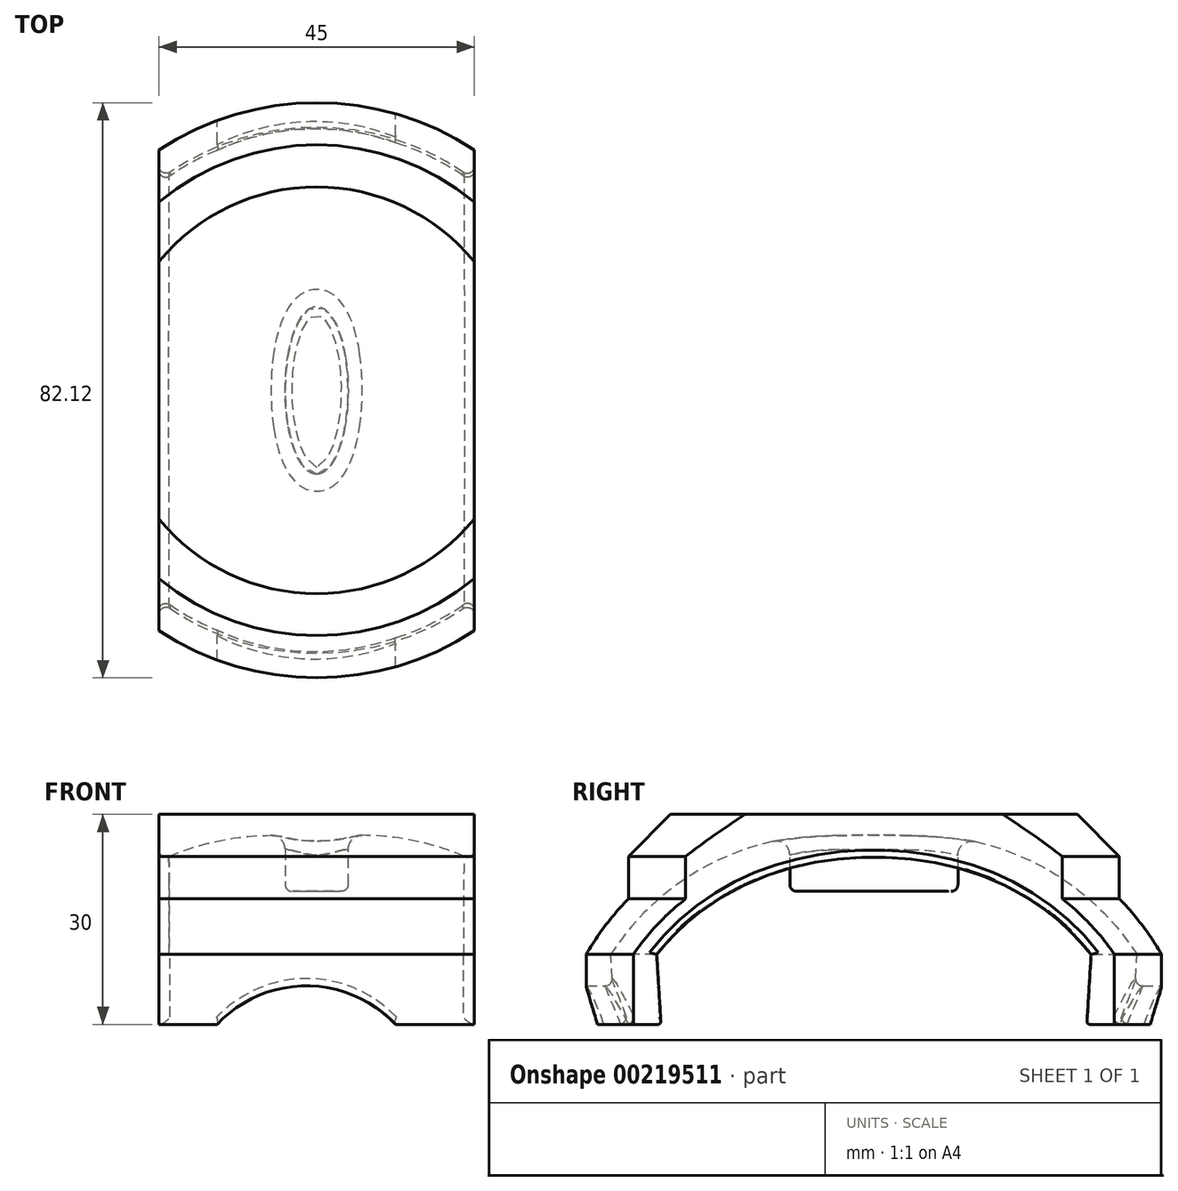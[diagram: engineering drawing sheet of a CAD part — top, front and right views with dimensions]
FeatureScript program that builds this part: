
annotation { "Feature Type Name" : "Feature", "Feature Type Description" : "" }
export const myFeature = defineFeature(function(context is Context, id is Id, definition is map)
    precondition{}
    {
        {
            var Q0;
            Q0=qCreatedBy(makeId("Top.planeOp"),FACE);
            var sketch = newSketch(context, id + "F0", { "sketchPlane" : qUnion([Q0])});
            skCircle(sketch, "E0", {"center": v(0, 0) * mm, "radius": 37.55 * mm});
            skSolve(sketch);
        }
        {
            var Q0;
            Q0=makeQuery(id+"F0.imprint","IMPRINT",FACE,{"disambiguationData":[TD([[makeQuery(id+"F0.imprint","IMPRINT",EDGE,{"derivedFrom":sQuery(id+"F0.wireOp",EDGE,"E0")}),1.0]])]});
            extrude(context, id + "F1", {"entities" : qUnion([Q0]), "depth" : 17 * mm});
        }
        {
            var Q0;
            Q0=makeQuery(id+"F1.opExtrude","CAP_EDGE",EDGE,{"disambiguationData":[OSD([sQuery(id+"F0.wireOp",EDGE,"E0")])],"isStart":false});
            fillet(context, id + "F2", {"entities" : qUnion([Q0]), "radius" : 37 * mm, "tangentPropagation" : true, "allowEdgeOverflow" : false});
        }
        {
            var Q0;
            Q0=makeQuery(id+"F1.opExtrude","CAP_FACE",FACE,{"disambiguationData":[OSD([sQuery(id+"F0.wireOp",EDGE,"E0")])],"isStart":true});
            shell(context, id + "F3", {"entities" : qUnion([Q0]), "thickness" : 3 * mm, "oppositeDirection" : true});
        }
        {
            var Q0;
            {var subQ0=sQuery(id+"F0.wireOp",EDGE,"E0");Q0=makeQuery(id+"F3.opShell","OFFSET_FACE",FACE,{"disambiguationData":[OSD([subQ0]),TDD([makeQuery(id+"F1.opExtrude","CAP_FACE",FACE,{"disambiguationData":[OSD([subQ0])],"isStart":false})])]});}
            var sketch = newSketch(context, id + "F4", { "sketchPlane" : qUnion([Q0])});
            skEllipse(sketch, "E1", {"center": v(0, 0) * mm, "majorRadius": 12 * mm, "minorRadius": 4.5 * mm, "majorAxis": v(0, 1)});
            skSolve(sketch);
        }
        {
            var Q0;
            {var subQ0=sQuery(id+"F4.wireOp",EDGE,"E1");var subQ1=sQuery(id+"F0.wireOp",EDGE,"E0");var subQ2=makeQuery(id+"F3.opShell","OFFSET_EDGE",EDGE,{"disambiguationData":[OSD([subQ1]),TDD([makeQuery(id+"F2.opFillet","BLEND_EDGE",EDGE,{"blendedFrom":[makeQuery(id+"F1.opExtrude","CAP_EDGE",EDGE,{"disambiguationData":[OSD([subQ1])],"isStart":false}),makeQuery(id+"F1.opExtrude","CAP_FACE",FACE,{"disambiguationData":[OSD([subQ1])],"isStart":false})],"blendedInto":[makeQuery(id+"F1.opExtrude","CAP_FACE",FACE,{"disambiguationData":[OSD([subQ1])],"isStart":false})]})])]});var subQ3=makeQuery(id+"F4.imprint","INTERSECT",VERTEX,{"disambiguationData":[OD(0.0)],"derivedFrom":[subQ2,subQ0]});Q0=makeQuery(id+"F4.imprint","IMPRINT",FACE,{"disambiguationData":[TD([[makeQuery(id+"F4.imprint","IMPRINT",EDGE,{"disambiguationData":[TD([[subQ3,-1.0]])],"derivedFrom":subQ0}),1.0]])]});}
            var Q1;
            {var subQ0=sQuery(id+"F4.wireOp",EDGE,"E1");var subQ1=sQuery(id+"F0.wireOp",EDGE,"E0");var subQ2=makeQuery(id+"F3.opShell","OFFSET_EDGE",EDGE,{"disambiguationData":[OSD([subQ1]),TDD([makeQuery(id+"F2.opFillet","BLEND_EDGE",EDGE,{"blendedFrom":[makeQuery(id+"F1.opExtrude","CAP_EDGE",EDGE,{"disambiguationData":[OSD([subQ1])],"isStart":false}),makeQuery(id+"F1.opExtrude","CAP_FACE",FACE,{"disambiguationData":[OSD([subQ1])],"isStart":false})],"blendedInto":[makeQuery(id+"F1.opExtrude","CAP_FACE",FACE,{"disambiguationData":[OSD([subQ1])],"isStart":false})]})])]});var subQ3=makeQuery(id+"F4.imprint","INTERSECT",VERTEX,{"disambiguationData":[OD(0.0)],"derivedFrom":[subQ2,subQ0]});Q1=makeQuery(id+"F4.imprint","IMPRINT",FACE,{"disambiguationData":[TD([[makeQuery(id+"F4.imprint","IMPRINT",EDGE,{"disambiguationData":[TD([[subQ3,1.0]])],"derivedFrom":subQ0}),1.0]])]});}
            var Q2;
            {var subQ0=sQuery(id+"F4.wireOp",EDGE,"E1");var subQ1=sQuery(id+"F0.wireOp",EDGE,"E0");var subQ2=makeQuery(id+"F3.opShell","OFFSET_EDGE",EDGE,{"disambiguationData":[OSD([subQ1]),TDD([makeQuery(id+"F2.opFillet","BLEND_EDGE",EDGE,{"blendedFrom":[makeQuery(id+"F1.opExtrude","CAP_EDGE",EDGE,{"disambiguationData":[OSD([subQ1])],"isStart":false}),makeQuery(id+"F1.opExtrude","CAP_FACE",FACE,{"disambiguationData":[OSD([subQ1])],"isStart":false})],"blendedInto":[makeQuery(id+"F1.opExtrude","CAP_FACE",FACE,{"disambiguationData":[OSD([subQ1])],"isStart":false})]})])]});var subQ3=makeQuery(id+"F4.imprint","INTERSECT",VERTEX,{"disambiguationData":[OD(1.0)],"derivedFrom":[subQ2,subQ0]});Q2=makeQuery(id+"F4.imprint","IMPRINT",FACE,{"disambiguationData":[TD([[makeQuery(id+"F4.imprint","IMPRINT",EDGE,{"disambiguationData":[TD([[subQ3,1.0]])],"derivedFrom":subQ0}),1.0]])]});}
            extrude(context, id + "F5", {"entities" : qUnion([Q0, Q1, Q2]), "operationType" : NewBodyOperationType.ADD, "depth" : 8 * mm});
        }
        {
            var Q0;
            Q0=makeQuery(id+"F1.opExtrude","CAP_FACE",FACE,{"disambiguationData":[OSD([sQuery(id+"F0.wireOp",EDGE,"E0")])],"isStart":true});
            var sketch = newSketch(context, id + "F6", { "sketchPlane" : qUnion([Q0])});
            skLineSegment(sketch, "E2", {"start": v(0, -41.06) * mm, "end": v(0, -41.06) * mm});
            skLineSegment(sketch, "E3", {"start": v(0, -41.06) * mm, "end": v(0, 41.06) * mm, "construction": true});
            skLineSegment(sketch, "E4", {"start": v(0, 0) * mm, "end": v(37.55, 0) * mm, "construction": true});
            skLineSegment(sketch, "E5", {"start": v(0, 0) * mm, "end": v(-37.55, 0) * mm, "construction": true});
            skLineSegment(sketch, "E6", {"start": v(0, 0) * mm, "end": v(12.69, 39.05) * mm, "construction": true});
            skLineSegment(sketch, "E7", {"start": v(0, 0) * mm, "end": v(-12.69, -39.05) * mm, "construction": true});
            skLineSegment(sketch, "E8", {"start": v(0, 0) * mm, "end": v(-12.69, 39.05) * mm, "construction": true});
            skLineSegment(sketch, "E9", {"start": v(0, 0) * mm, "end": v(12.69, -39.05) * mm, "construction": true});
            skLineSegment(sketch, "E10", {"start": v(37.55, 0) * mm, "end": v(41.06, 0) * mm, "construction": true});
            skLineSegment(sketch, "E11", {"start": v(-37.55, 0) * mm, "end": v(-41.06, 0) * mm, "construction": true});
            skSolve(sketch);
        }
        {
            var Q0;
            Q0=qCreatedBy(makeId("Front.planeOp"),FACE);
            var sketch = newSketch(context, id + "F7", { "sketchPlane" : qUnion([Q0])});
            skLineSegment(sketch, "E12", {"start": v(41.06, 0) * mm, "end": v(41.06, -10) * mm});
            skLineSegment(sketch, "E13", {"start": v(41.06, -10) * mm, "end": v(37.55, -10) * mm});
            skLineSegment(sketch, "E14", {"start": v(37.05, -10) * mm, "end": v(37.55, 0) * mm});
            skLineSegment(sketch, "E15", {"start": v(37.55, 0) * mm, "end": v(41.06, 0) * mm});
            skLineSegment(sketch, "E16", {"start": v(37.55, 0) * mm, "end": v(37.55, -10) * mm});
            skLineSegment(sketch, "E17", {"start": v(37.55, -10) * mm, "end": v(37.05, -10) * mm});
            skLineSegment(sketch, "E18", {"start": v(0, 0) * mm, "end": v(0, -14.5) * mm, "construction": true});
            skSolve(sketch);
        }
        {
            var Q0;
            {var subQ0=makeQuery(id+"FDc1g6xEYOhVyaV_1.opRevolve","SWEPT_EDGE",EDGE,{"disambiguationData":[OSD([sQuery(id+"F7.wireOp",EDGE,"E12"),sQuery(id+"F7.wireOp",EDGE,"E13")])]});Q0=makeQuery(id+"FIxkV1x1mZ7Anp5_2.boolean.opBoolean","MERGE",EDGE,{"derivedFrom":[subQ0,makeQuery(id+"FIxkV1x1mZ7Anp5_2.opPattern","COPY",EDGE,{"derivedFrom":subQ0,"instanceName":"1"})]});}
            var Q1;
            Q1=makeQuery(id+"F5.opExtrude","CAP_EDGE",EDGE,{"disambiguationData":[OSD([sQuery(id+"F4.wireOp",EDGE,"E1")])],"isStart":false});
            fillet(context, id + "F8", {"entities" : qUnion([Q0, Q1]), "radius" : 1 * mm, "tangentPropagation" : true, "allowEdgeOverflow" : false});
        }
        {
            var Q0;
            Q0=makeQuery(id+"F1.opExtrude","CAP_FACE",FACE,{"disambiguationData":[OSD([sQuery(id+"F0.wireOp",EDGE,"E0")])],"isStart":false});
            var sketch = newSketch(context, id + "F9", { "sketchPlane" : qUnion([Q0])});
            skCircle(sketch, "E19", {"center": v(0, 0) * mm, "radius": 35.05 * mm});
            skSolve(sketch);
        }
        {
            var Q0;
            Q0=makeQuery(id+"F9.imprint","IMPRINT",FACE,{"disambiguationData":[TD([[makeQuery(id+"F9.imprint","IMPRINT",EDGE,{"derivedFrom":sQuery(id+"F9.wireOp",EDGE,"E19")}),1.0]])]});
            extrude(context, id + "F10", {"entities" : qUnion([Q0]), "operationType" : NewBodyOperationType.ADD, "endBound" : BoundingType.UP_TO_NEXT, "oppositeDirection" : true, "depth" : 25 * mm});
        }
        {
            var Q0;
            Q0=makeQuery(id+"F10.opExtrude","CAP_EDGE",EDGE,{"disambiguationData":[OSD([sQuery(id+"F9.wireOp",EDGE,"E19")])],"isStart":true});
            chamfer(context, id + "F11", {"entities" : qUnion([Q0]), "width" : 6 * mm, "tangentPropagation" : true});
        }
        {
            var Q0;
            Q0=makeQuery(id+"F7.imprint","IMPRINT",FACE,{"disambiguationData":[TD([[makeQuery(id+"F7.imprint","IMPRINT",EDGE,{"derivedFrom":sQuery(id+"F7.wireOp",EDGE,"E12")}),-1.0]])]});
            var Q1;
            Q1=makeQuery(id+"F7.imprint","IMPRINT",FACE,{"disambiguationData":[TD([[makeQuery(id+"F7.imprint","IMPRINT",EDGE,{"derivedFrom":sQuery(id+"F7.wireOp",EDGE,"E14")}),-1.0]])]});
            var Q2;
            Q2=sQuery(id+"F7.wireOp",EDGE,"E18");
            revolve(context, id + "F12", {"operationType" : NewBodyOperationType.ADD, "entities" : qUnion([Q0, Q1]), "axis" : qUnion([Q2]), "revolveType" : RevolveType.FULL});
        }
        {
            var Q0;
            Q0=qCreatedBy(makeId("Right.planeOp"),FACE);
            cPlane(context, id + "F13", {"entities" : qUnion([Q0]), "cplaneType" : CPlaneType.OFFSET, "offset" : 22.5 * mm, "width" : 150 * mm, "height" : 150 * mm});
        }
        {
            var Q0;
            Q0=qCreatedBy(id+"F13.planeOp",FACE);
            var sketch = newSketch(context, id + "F14", { "sketchPlane" : qUnion([Q0])});
            skLineSegment(sketch, "E20.bottom", {"start": v(-41.47, -13.51) * mm, "end": v(42.62, -13.51) * mm});
            skLineSegment(sketch, "E20.top", {"start": v(-41.47, 26.02) * mm, "end": v(42.62, 26.02) * mm});
            skLineSegment(sketch, "E20.left", {"start": v(-41.47, -13.51) * mm, "end": v(-41.47, 26.02) * mm});
            skLineSegment(sketch, "E20.right", {"start": v(42.62, -13.51) * mm, "end": v(42.62, 26.02) * mm});
            skSolve(sketch);
        }
        {
            var Q0;
            Q0=makeQuery(id+"F14.imprint","IMPRINT",FACE,{"disambiguationData":[TD([[makeQuery(id+"F14.imprint","IMPRINT",EDGE,{"derivedFrom":sQuery(id+"F14.wireOp",EDGE,"E20.bottom")}),1.0]])]});
            extrude(context, id + "F15", {"entities" : qUnion([Q0]), "operationType" : NewBodyOperationType.REMOVE, "depth" : 25 * mm});
        }
        {
            var Q0;
            Q0=qCreatedBy(id+"F13.planeOp",FACE);
            cPlane(context, id + "F16", {"entities" : qUnion([Q0]), "cplaneType" : CPlaneType.OFFSET, "offset" : 45 * mm, "oppositeDirection" : true, "width" : 150 * mm, "height" : 150 * mm});
        }
        {
            var Q0;
            Q0=qCreatedBy(id+"F16.planeOp",FACE);
            var sketch = newSketch(context, id + "F17", { "sketchPlane" : qUnion([Q0])});
            skLineSegment(sketch, "E21.bottom", {"start": v(-41.2, -27.17) * mm, "end": v(38.42, -27.17) * mm});
            skLineSegment(sketch, "E21.top", {"start": v(-41.2, 30) * mm, "end": v(38.42, 30) * mm});
            skLineSegment(sketch, "E21.left", {"start": v(-41.2, -27.17) * mm, "end": v(-41.2, 30) * mm});
            skLineSegment(sketch, "E21.right", {"start": v(38.42, -27.17) * mm, "end": v(38.42, 30) * mm});
            skSolve(sketch);
        }
        {
            var Q0;
            Q0=makeQuery(id+"F17.imprint","IMPRINT",FACE,{"disambiguationData":[TD([[makeQuery(id+"F17.imprint","IMPRINT",EDGE,{"derivedFrom":sQuery(id+"F17.wireOp",EDGE,"E21.bottom")}),1.0]])]});
            extrude(context, id + "F18", {"entities" : qUnion([Q0]), "operationType" : NewBodyOperationType.REMOVE, "oppositeDirection" : true, "depth" : 25 * mm});
        }
        {
            var Q0;
            Q0=qCreatedBy(makeId("Front.planeOp"),FACE);
            var sketch = newSketch(context, id + "F19", { "sketchPlane" : qUnion([Q0])});
            skCircle(sketch, "E22", {"center": v(-1.48, -22) * mm, "radius": 17.5 * mm});
            skSolve(sketch);
        }
        {
            var Q0;
            Q0=makeQuery(id+"F19.imprint","IMPRINT",FACE,{"disambiguationData":[TD([[makeQuery(id+"F19.imprint","IMPRINT",EDGE,{"derivedFrom":sQuery(id+"F19.wireOp",EDGE,"E22")}),1.0]])]});
            extrude(context, id + "F20", {"entities" : qUnion([Q0]), "operationType" : NewBodyOperationType.REMOVE, "endBound" : BoundingType.SYMMETRIC, "depth" : 117.8 * mm});
        }
        {
            var Q0;
            {var subQ0=sQuery(id+"F7.wireOp",EDGE,"E17");var subQ1=sQuery(id+"F7.wireOp",EDGE,"E14");Q0=makeQuery(id+"F20.boolean.opBoolean","SPLIT",EDGE,{"disambiguationData":[TD([makeQuery(id+"F18.boolean.opBoolean","COPY",FACE,{"derivedFrom":makeQuery(id+"F18.opExtrude","CAP_FACE",FACE,{"disambiguationData":[OSD([sQuery(id+"F17.wireOp",EDGE,"E21.bottom"),sQuery(id+"F17.wireOp",EDGE,"E21.top"),sQuery(id+"F17.wireOp",EDGE,"E21.left"),sQuery(id+"F17.wireOp",EDGE,"E21.right")])],"isStart":true})})])],"derivedFrom":makeQuery(id+"F18.boolean.opBoolean","SPLIT",EDGE,{"disambiguationData":[OD(1.0)],"derivedFrom":makeQuery(id+"F12.opRevolve","SWEPT_EDGE",EDGE,{"disambiguationData":[OSD([subQ1,subQ0])]})})});}
            var Q1;
            Q1=makeQuery(id+"F20.boolean.opBoolean","INTERSECT",EDGE,{"derivedFrom":[makeQuery(id+"F18.boolean.opBoolean","SPLIT",FACE,{"disambiguationData":[OD(1.0)],"derivedFrom":makeQuery(id+"F12.opRevolve","SWEPT_FACE",FACE,{"disambiguationData":[OSD([sQuery(id+"F7.wireOp",EDGE,"E14")])]})}),makeQuery(id+"F20.opExtrude","SWEPT_FACE",FACE,{"disambiguationData":[OSD([sQuery(id+"F19.wireOp",EDGE,"E22")])]})]});
            var Q2;
            {var subQ0=sQuery(id+"F7.wireOp",EDGE,"E17");var subQ1=sQuery(id+"F7.wireOp",EDGE,"E14");Q2=makeQuery(id+"F20.boolean.opBoolean","SPLIT",EDGE,{"disambiguationData":[TD([makeQuery(id+"F15.boolean.opBoolean","COPY",FACE,{"derivedFrom":makeQuery(id+"F15.opExtrude","CAP_FACE",FACE,{"disambiguationData":[OSD([sQuery(id+"F14.wireOp",EDGE,"E20.bottom"),sQuery(id+"F14.wireOp",EDGE,"E20.top"),sQuery(id+"F14.wireOp",EDGE,"E20.left"),sQuery(id+"F14.wireOp",EDGE,"E20.right")])],"isStart":true})})])],"derivedFrom":makeQuery(id+"F18.boolean.opBoolean","SPLIT",EDGE,{"disambiguationData":[OD(1.0)],"derivedFrom":makeQuery(id+"F12.opRevolve","SWEPT_EDGE",EDGE,{"disambiguationData":[OSD([subQ1,subQ0])]})})});}
            var Q3;
            {var subQ0=sQuery(id+"F7.wireOp",EDGE,"E17");var subQ1=sQuery(id+"F7.wireOp",EDGE,"E14");Q3=makeQuery(id+"F20.boolean.opBoolean","SPLIT",EDGE,{"disambiguationData":[TD([makeQuery(id+"F18.boolean.opBoolean","COPY",FACE,{"derivedFrom":makeQuery(id+"F18.opExtrude","CAP_FACE",FACE,{"disambiguationData":[OSD([sQuery(id+"F17.wireOp",EDGE,"E21.bottom"),sQuery(id+"F17.wireOp",EDGE,"E21.top"),sQuery(id+"F17.wireOp",EDGE,"E21.left"),sQuery(id+"F17.wireOp",EDGE,"E21.right")])],"isStart":true})})])],"derivedFrom":makeQuery(id+"F18.boolean.opBoolean","SPLIT",EDGE,{"disambiguationData":[OD(0.0)],"derivedFrom":makeQuery(id+"F12.opRevolve","SWEPT_EDGE",EDGE,{"disambiguationData":[OSD([subQ1,subQ0])]})})});}
            var Q4;
            Q4=makeQuery(id+"F20.boolean.opBoolean","INTERSECT",EDGE,{"derivedFrom":[makeQuery(id+"F18.boolean.opBoolean","SPLIT",FACE,{"disambiguationData":[OD(0.0)],"derivedFrom":makeQuery(id+"F12.opRevolve","SWEPT_FACE",FACE,{"disambiguationData":[OSD([sQuery(id+"F7.wireOp",EDGE,"E14")])]})}),makeQuery(id+"F20.opExtrude","SWEPT_FACE",FACE,{"disambiguationData":[OSD([sQuery(id+"F19.wireOp",EDGE,"E22")])]})]});
            var Q5;
            {var subQ0=sQuery(id+"F7.wireOp",EDGE,"E17");var subQ1=sQuery(id+"F7.wireOp",EDGE,"E14");Q5=makeQuery(id+"F20.boolean.opBoolean","SPLIT",EDGE,{"disambiguationData":[TD([makeQuery(id+"F15.boolean.opBoolean","COPY",FACE,{"derivedFrom":makeQuery(id+"F15.opExtrude","CAP_FACE",FACE,{"disambiguationData":[OSD([sQuery(id+"F14.wireOp",EDGE,"E20.bottom"),sQuery(id+"F14.wireOp",EDGE,"E20.top"),sQuery(id+"F14.wireOp",EDGE,"E20.left"),sQuery(id+"F14.wireOp",EDGE,"E20.right")])],"isStart":true})})])],"derivedFrom":makeQuery(id+"F18.boolean.opBoolean","SPLIT",EDGE,{"disambiguationData":[OD(0.0)],"derivedFrom":makeQuery(id+"F12.opRevolve","SWEPT_EDGE",EDGE,{"disambiguationData":[OSD([subQ1,subQ0])]})})});}
            var Q6;
            {var subQ0=sQuery(id+"F0.wireOp",EDGE,"E0");Q6=makeQuery(id+"F15.boolean.opBoolean","INTERSECT",EDGE,{"derivedFrom":[makeQuery(id+"F3.opShell","OFFSET_FACE",FACE,{"disambiguationData":[OSD([subQ0]),TDD([makeQuery(id+"F2.opFillet","BLEND_FACE",FACE,{"disambiguationData":[OSD([subQ0])]})])]}),makeQuery(id+"F15.opExtrude","CAP_FACE",FACE,{"disambiguationData":[OSD([sQuery(id+"F14.wireOp",EDGE,"E20.bottom"),sQuery(id+"F14.wireOp",EDGE,"E20.top"),sQuery(id+"F14.wireOp",EDGE,"E20.left"),sQuery(id+"F14.wireOp",EDGE,"E20.right")])],"isStart":true})]});}
            var Q7;
            Q7=makeQuery(id+"F15.boolean.opBoolean","INTERSECT",EDGE,{"disambiguationData":[OD(1.0)],"derivedFrom":[makeQuery(id+"F12.opRevolve","SWEPT_FACE",FACE,{"disambiguationData":[OSD([sQuery(id+"F7.wireOp",EDGE,"E14")])]}),makeQuery(id+"F15.opExtrude","CAP_FACE",FACE,{"disambiguationData":[OSD([sQuery(id+"F14.wireOp",EDGE,"E20.bottom"),sQuery(id+"F14.wireOp",EDGE,"E20.top"),sQuery(id+"F14.wireOp",EDGE,"E20.left"),sQuery(id+"F14.wireOp",EDGE,"E20.right")])],"isStart":true})]});
            var Q8;
            Q8=makeQuery(id+"F15.boolean.opBoolean","INTERSECT",EDGE,{"disambiguationData":[OD(0.0)],"derivedFrom":[makeQuery(id+"F12.opRevolve","SWEPT_FACE",FACE,{"disambiguationData":[OSD([sQuery(id+"F7.wireOp",EDGE,"E14")])]}),makeQuery(id+"F15.opExtrude","CAP_FACE",FACE,{"disambiguationData":[OSD([sQuery(id+"F14.wireOp",EDGE,"E20.bottom"),sQuery(id+"F14.wireOp",EDGE,"E20.top"),sQuery(id+"F14.wireOp",EDGE,"E20.left"),sQuery(id+"F14.wireOp",EDGE,"E20.right")])],"isStart":true})]});
            var Q9;
            Q9=makeQuery(id+"F18.boolean.opBoolean","INTERSECT",EDGE,{"disambiguationData":[OD(1.0)],"derivedFrom":[makeQuery(id+"F12.opRevolve","SWEPT_FACE",FACE,{"disambiguationData":[OSD([sQuery(id+"F7.wireOp",EDGE,"E14")])]}),makeQuery(id+"F18.opExtrude","CAP_FACE",FACE,{"disambiguationData":[OSD([sQuery(id+"F17.wireOp",EDGE,"E21.bottom"),sQuery(id+"F17.wireOp",EDGE,"E21.top"),sQuery(id+"F17.wireOp",EDGE,"E21.left"),sQuery(id+"F17.wireOp",EDGE,"E21.right")])],"isStart":true})]});
            var Q10;
            {var subQ0=sQuery(id+"F0.wireOp",EDGE,"E0");Q10=makeQuery(id+"F18.boolean.opBoolean","INTERSECT",EDGE,{"derivedFrom":[makeQuery(id+"F3.opShell","OFFSET_FACE",FACE,{"disambiguationData":[OSD([subQ0]),TDD([makeQuery(id+"F2.opFillet","BLEND_FACE",FACE,{"disambiguationData":[OSD([subQ0])]})])]}),makeQuery(id+"F18.opExtrude","CAP_FACE",FACE,{"disambiguationData":[OSD([sQuery(id+"F17.wireOp",EDGE,"E21.bottom"),sQuery(id+"F17.wireOp",EDGE,"E21.top"),sQuery(id+"F17.wireOp",EDGE,"E21.left"),sQuery(id+"F17.wireOp",EDGE,"E21.right")])],"isStart":true})]});}
            var Q11;
            Q11=makeQuery(id+"F18.boolean.opBoolean","INTERSECT",EDGE,{"disambiguationData":[OD(0.0)],"derivedFrom":[makeQuery(id+"F12.opRevolve","SWEPT_FACE",FACE,{"disambiguationData":[OSD([sQuery(id+"F7.wireOp",EDGE,"E14")])]}),makeQuery(id+"F18.opExtrude","CAP_FACE",FACE,{"disambiguationData":[OSD([sQuery(id+"F17.wireOp",EDGE,"E21.bottom"),sQuery(id+"F17.wireOp",EDGE,"E21.top"),sQuery(id+"F17.wireOp",EDGE,"E21.left"),sQuery(id+"F17.wireOp",EDGE,"E21.right")])],"isStart":true})]});
            fillet(context, id + "F21", {"entities" : qUnion([Q0, Q1, Q2, Q3, Q4, Q5, Q6, Q7, Q8, Q9, Q10, Q11]), "radius" : 1 * mm, "tangentPropagation" : true, "allowEdgeOverflow" : false});
        }
        {
            var Q0;
            {var subQ0=sQuery(id+"F0.wireOp",EDGE,"E0");Q0=makeQuery(id+"F5.boolean.opBoolean","INTERSECT",EDGE,{"disambiguationData":[OD(0.0)],"derivedFrom":[makeQuery(id+"F3.opShell","OFFSET_FACE",FACE,{"disambiguationData":[OSD([subQ0]),TDD([makeQuery(id+"F2.opFillet","BLEND_FACE",FACE,{"disambiguationData":[OSD([subQ0])]})])]}),makeQuery(id+"F5.opExtrude","SWEPT_FACE",FACE,{"disambiguationData":[OSD([sQuery(id+"F4.wireOp",EDGE,"E1")])]})]});}
            var Q1;
            Q1=makeQuery(id+"F5.boolean.opBoolean","SPLIT",EDGE,{"disambiguationData":[OD(1.0)],"derivedFrom":makeQuery(id+"F5.opExtrude","CAP_EDGE",EDGE,{"disambiguationData":[OSD([sQuery(id+"F4.wireOp",EDGE,"E1")])],"isStart":true})});
            fillet(context, id + "F22", {"entities" : qUnion([Q0, Q1]), "radius" : 2 * mm, "tangentPropagation" : true, "allowEdgeOverflow" : false});
        }
    });
